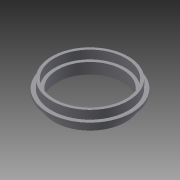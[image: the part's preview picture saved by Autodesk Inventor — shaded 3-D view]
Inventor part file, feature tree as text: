
AUTODESK INVENTOR PART (.ipt)
format: ipt  version: 2013 (Build 170138000, 138)  size: 116,736 bytes
history: native  units: mm
features: extrude x3, sketch x3
ambient origin geometry x8: Origin, YZ Plane, XZ Plane, XY Plane, X Axis, Y Axis, Z Axis, Center Point
bodies: Solid1 (feature_tree)
feature tree (6):
  extrude  "Extrusion1"  Depth=25.4mm
  extrude  "Extrusion3"  Depth=23.0mm
  extrude  "Extrusion4"  Depth=1.0mm TaperAngle=0.0deg
  sketch  "Sketch1"  dims[d3=1.0mm d4=25.4mm]
  sketch  "Sketch3"  dims[d5=3.0mm d6=0.0mm d12=23.0mm]
  sketch  "Sketch4"  dims[d14=29.8mm d15=1.0mm d16=0.0mm d17=1.0mm d19=25.2mm d20=3.0mm d21=0.0mm]
